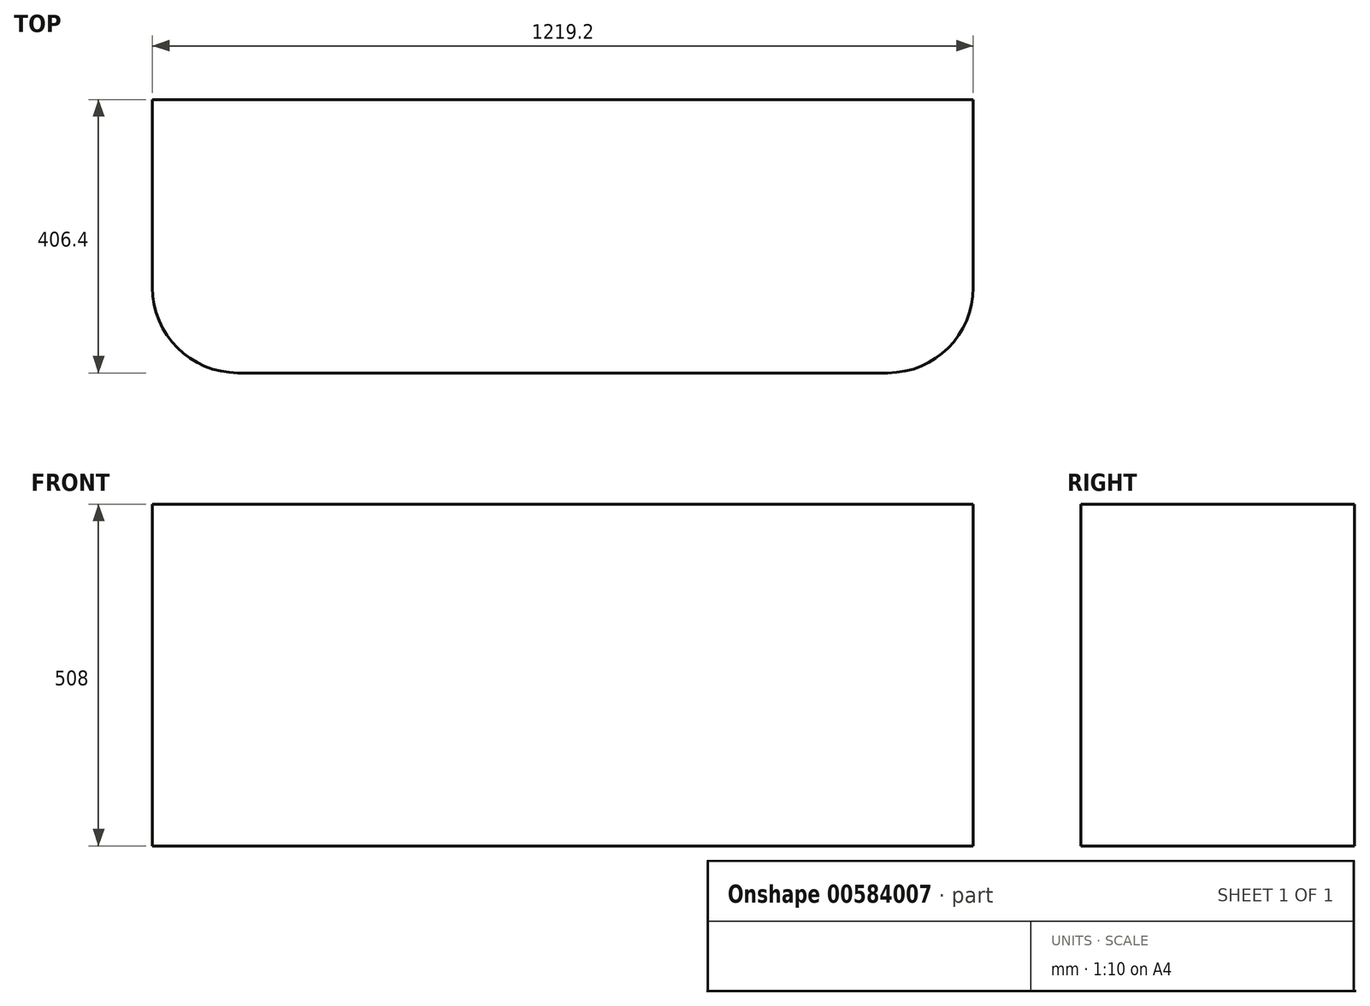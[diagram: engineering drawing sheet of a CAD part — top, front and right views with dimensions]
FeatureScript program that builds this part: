
annotation { "Feature Type Name" : "Feature", "Feature Type Description" : "" }
export const myFeature = defineFeature(function(context is Context, id is Id, definition is map)
    precondition{}
    {
        {
            var Q0;
            Q0=qCreatedBy(makeId("Top.planeOp"),FACE);
            var sketch = newSketch(context, id + "F0", { "sketchPlane" : qUnion([Q0])});
            skLineSegment(sketch, "E0.bottom", {"start": v(-604.64, 79.53) * mm, "end": v(614.56, 79.53) * mm});
            skLineSegment(sketch, "E0.top", {"start": v(-604.64, -326.87) * mm, "end": v(614.56, -326.87) * mm});
            skLineSegment(sketch, "E0.left", {"start": v(-604.64, 79.53) * mm, "end": v(-604.64, -326.87) * mm});
            skLineSegment(sketch, "E0.right", {"start": v(614.56, 79.53) * mm, "end": v(614.56, -326.87) * mm});
            skSolve(sketch);
        }
        {
            var Q0;
            Q0=makeQuery(id+"F0.imprint","IMPRINT",FACE,{"disambiguationData":[TD([[makeQuery(id+"F0.imprint","IMPRINT",EDGE,{"derivedFrom":sQuery(id+"F0.wireOp",EDGE,"E0.bottom")}),-1.0]])]});
            extrude(context, id + "F1", {"entities" : qUnion([Q0]), "depth" : 508 * mm, "offsetDistance" : 25.4 * mm});
        }
        {
            var Q0;
            Q0=makeQuery(id+"F1.opExtrude","SWEPT_EDGE",EDGE,{"disambiguationData":[OSD([sQuery(id+"F0.wireOp",EDGE,"E0.top"),sQuery(id+"F0.wireOp",EDGE,"E0.left")])]});
            var Q1;
            Q1=makeQuery(id+"F1.opExtrude","SWEPT_EDGE",EDGE,{"disambiguationData":[OSD([sQuery(id+"F0.wireOp",EDGE,"E0.top"),sQuery(id+"F0.wireOp",EDGE,"E0.right")])]});
            fillet(context, id + "F2", {"entities" : qUnion([Q0, Q1]), "radius" : 127 * mm, "tangentPropagation" : true, "allowEdgeOverflow" : false});
        }
    });
